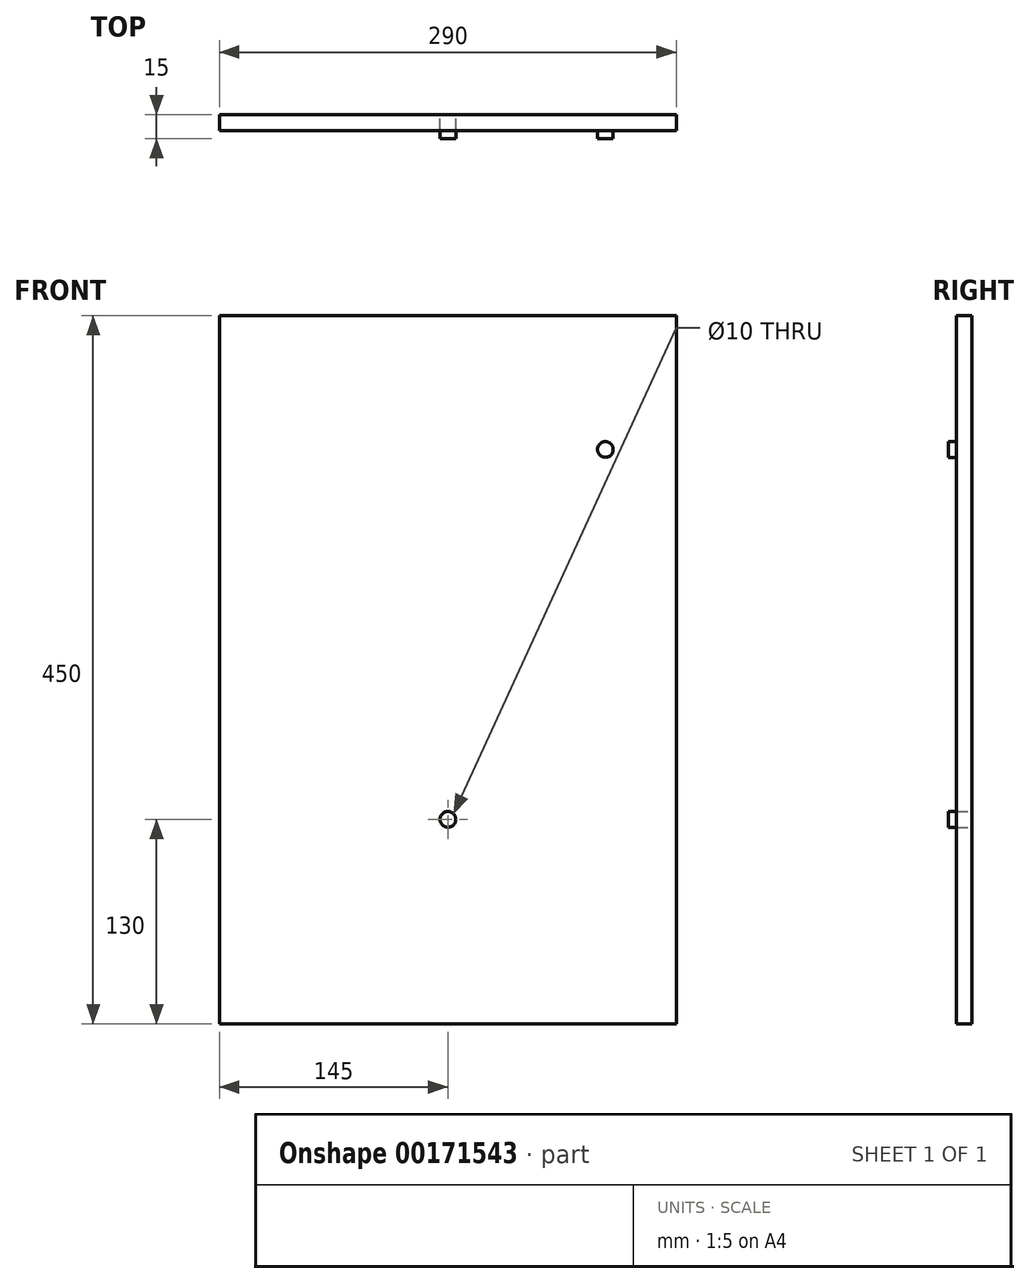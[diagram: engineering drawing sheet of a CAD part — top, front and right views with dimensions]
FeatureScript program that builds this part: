
annotation { "Feature Type Name" : "Feature", "Feature Type Description" : "" }
export const myFeature = defineFeature(function(context is Context, id is Id, definition is map)
    precondition{}
    {
        {
            var Q0;
            Q0=qCreatedBy(makeId("Front.planeOp"),FACE);
            var sketch = newSketch(context, id + "F0", { "sketchPlane" : qUnion([Q0])});
            skLineSegment(sketch, "E0.bottom", {"start": v(145, 225) * mm, "end": v(-145, 225) * mm});
            skLineSegment(sketch, "E0.top", {"start": v(145, -225) * mm, "end": v(-145, -225) * mm});
            skLineSegment(sketch, "E0.left", {"start": v(145, 225) * mm, "end": v(145, -225) * mm});
            skLineSegment(sketch, "E0.right", {"start": v(-145, 225) * mm, "end": v(-145, -225) * mm});
            skPoint(sketch, "E0.middle", {"position": v(0, 0) * mm});
            skCircle(sketch, "E1", {"center": v(100, 140) * mm, "radius": 19 * mm, "construction": true});
            skCircle(sketch, "E2", {"center": v(0, -95) * mm, "radius": 19 * mm, "construction": true});
            skLineSegment(sketch, "E3", {"start": v(0, -95) * mm, "end": v(145, -95) * mm, "construction": true});
            skLineSegment(sketch, "E4", {"start": v(0, -95) * mm, "end": v(100, 140) * mm, "construction": true});
            skCircle(sketch, "E5", {"center": v(100, 140) * mm, "radius": 5 * mm});
            skCircle(sketch, "E6", {"center": v(0, -95) * mm, "radius": 5 * mm});
            skPoint(sketch, "E7", {"position": v(100, 159) * mm});
            skPoint(sketch, "E8", {"position": v(0, -114) * mm});
            skSolve(sketch);
        }
        {
            var Q0;
            Q0=qSketchRegion(id+"F0",true);
            extrude(context, id + "F1", {"entities" : qUnion([Q0]), "depth" : 10 * mm});
        }
        {
            var Q0;
            Q0=makeQuery(id+"F0.imprint","IMPRINT",FACE,{"disambiguationData":[TD([[makeQuery(id+"F0.imprint","IMPRINT",EDGE,{"derivedFrom":sQuery(id+"F0.wireOp",EDGE,"E5")}),1.0]])]});
            extrude(context, id + "F2", {"entities" : qUnion([Q0]), "operationType" : NewBodyOperationType.ADD, "depth" : 15 * mm});
        }
        {
            var Q0;
            Q0=makeQuery(id+"F0.imprint","IMPRINT",FACE,{"disambiguationData":[TD([[makeQuery(id+"F0.imprint","IMPRINT",EDGE,{"derivedFrom":sQuery(id+"F0.wireOp",EDGE,"E6")}),1.0]])]});
            extrude(context, id + "F3", {"entities" : qUnion([Q0]), "depth" : 15 * mm});
        }
    });
